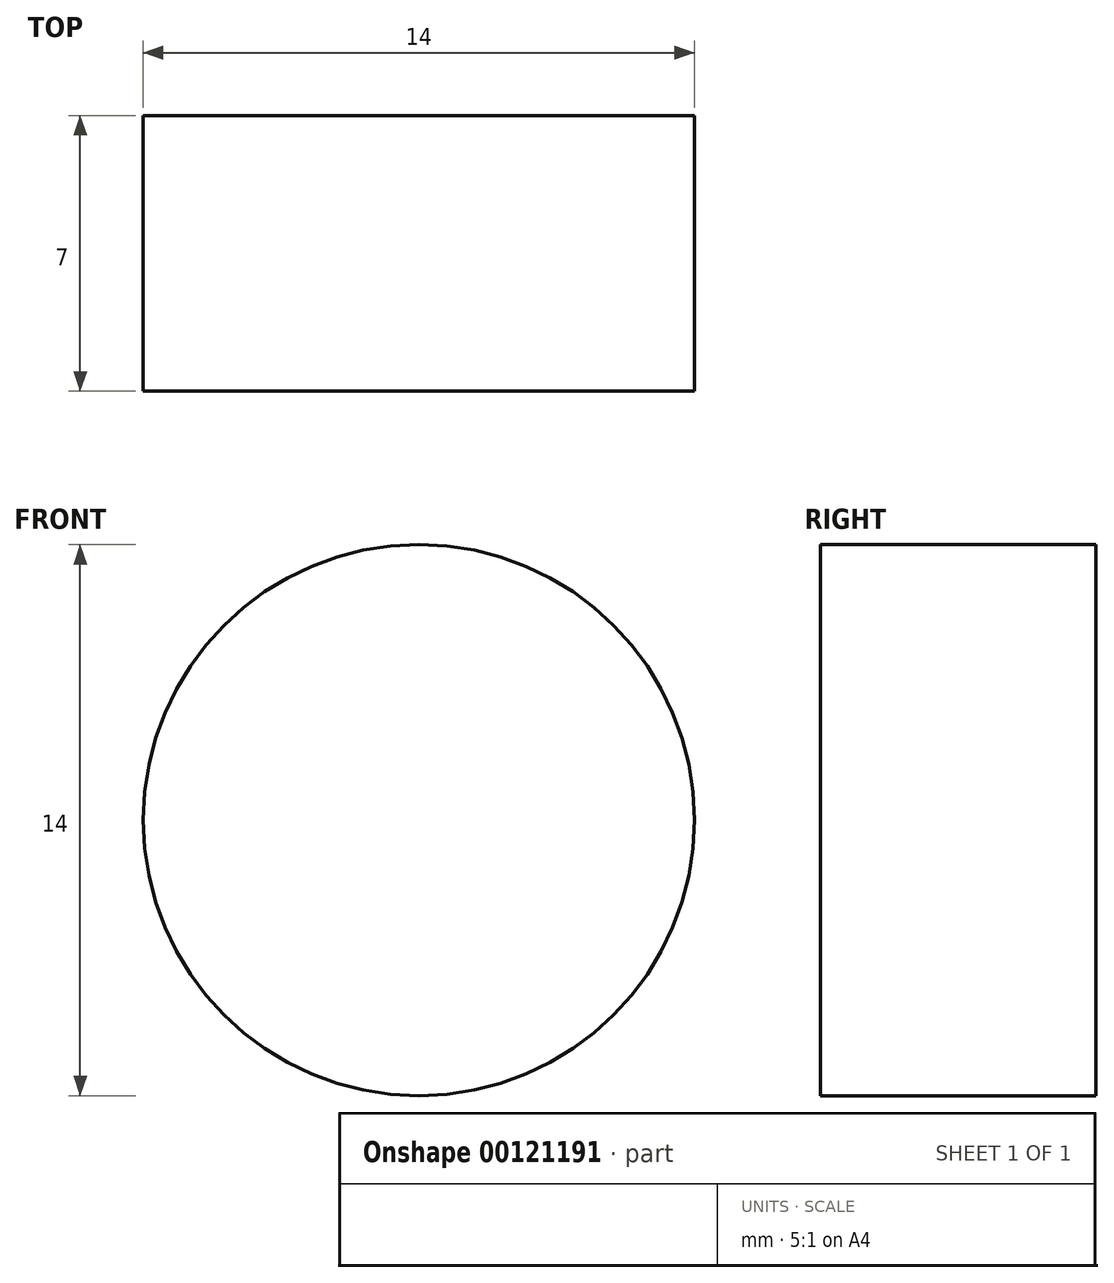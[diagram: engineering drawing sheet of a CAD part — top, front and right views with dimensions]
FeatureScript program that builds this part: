
annotation { "Feature Type Name" : "Feature", "Feature Type Description" : "" }
export const myFeature = defineFeature(function(context is Context, id is Id, definition is map)
    precondition{}
    {
        {
            var Q0;
            Q0=qCreatedBy(makeId("Front.planeOp"),FACE);
            var sketch = newSketch(context, id + "F0", { "sketchPlane" : qUnion([Q0])});
            skCircle(sketch, "E0", {"center": v(0, 0) * mm, "radius": 7 * mm});
            skSolve(sketch);
        }
        {
            var Q0;
            Q0=qSketchRegion(id+"F0",true);
            extrude(context, id + "F1", {"entities" : qUnion([Q0]), "depth" : 7 * mm});
        }
    });
